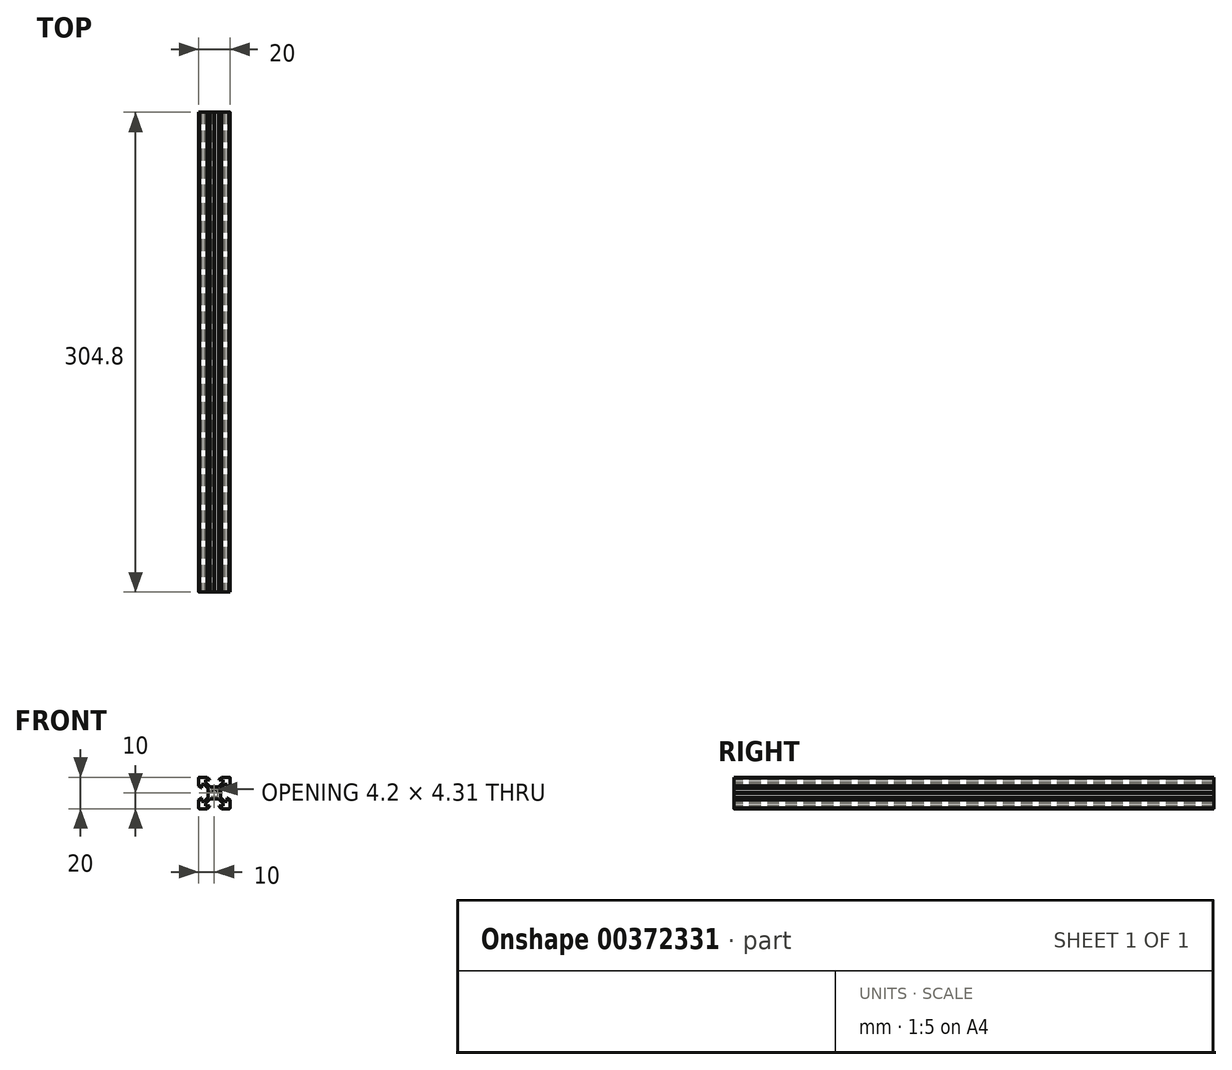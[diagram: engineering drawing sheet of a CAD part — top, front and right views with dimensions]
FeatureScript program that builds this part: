
annotation { "Feature Type Name" : "Feature", "Feature Type Description" : "" }
export const myFeature = defineFeature(function(context is Context, id is Id, definition is map)
    precondition{}
    {
        {
            var Q0;
            Q0=qCreatedBy(makeId("Front.planeOp"),FACE);
            var sketch = newSketch(context, id + "F0", { "sketchPlane" : qUnion([Q0])});
            skFitSpline(sketch, "E0.0", {"points": [v(-8.2, 3.13) * mm, v(-8.2, 3.92) * mm, v(-8.2, 4.7) * mm, v(-8.2, 5.5) * mm]});
            skFitSpline(sketch, "E0.1", {"points": [v(-8.2, 5.5) * mm, v(-7.65, 5.5) * mm, v(-7.1, 5.5) * mm, v(-6.56, 5.5) * mm]});
            skFitSpline(sketch, "E0.2", {"points": [v(-6.56, 5.5) * mm, v(-5.67, 4.61) * mm, v(-4.79, 3.73) * mm, v(-3.9, 2.84) * mm]});
            skFitSpline(sketch, "E0.3", {"points": [v(-2.84, 3.9) * mm, v(-3.73, 4.79) * mm, v(-4.61, 5.67) * mm, v(-5.5, 6.56) * mm]});
            skFitSpline(sketch, "E0.4", {"points": [v(-5.5, 6.56) * mm, v(-5.5, 7.1) * mm, v(-5.5, 7.65) * mm, v(-5.5, 8.2) * mm]});
            skFitSpline(sketch, "E0.5", {"points": [v(-5.5, 8.2) * mm, v(-4.7, 8.2) * mm, v(-3.92, 8.2) * mm, v(-3.12, 8.2) * mm]});
            skFitSpline(sketch, "E0.6", {"points": [v(-3.12, 8.2) * mm, v(-3.12, 8.32) * mm, v(-3.12, 8.43) * mm, v(-3.12, 8.55) * mm]});
            skFitSpline(sketch, "E0.7", {"points": [v(-10, 4.58) * mm, v(-9.51, 4.1) * mm, v(-9.03, 3.61) * mm, v(-8.54, 3.13) * mm]});
            skFitSpline(sketch, "E0.8", {"points": [v(-8.54, 3.13) * mm, v(-8.43, 3.13) * mm, v(-8.31, 3.13) * mm, v(-8.2, 3.13) * mm]});
            skFitSpline(sketch, "E0.9", {"points": [v(-10, 9.5) * mm, v(-10, 7.86) * mm, v(-10, 6.22) * mm, v(-10, 4.58) * mm]});
            skFitSpline(sketch, "E0.10", {"points": [v(-9.5, 10) * mm, v(-9.57, 10) * mm, v(-9.63, 9.99) * mm, v(-9.7, 9.96) * mm, v(-9.75, 9.94) * mm, v(-9.8, 9.9) * mm, v(-9.85, 9.85) * mm, v(-9.9, 9.8) * mm, v(-9.94, 9.75) * mm, v(-9.96, 9.7) * mm, v(-9.99, 9.63) * mm, v(-10, 9.57) * mm, v(-10, 9.5) * mm]});
            skFitSpline(sketch, "E0.11", {"points": [v(-4.58, 10) * mm, v(-6.22, 10) * mm, v(-7.86, 10) * mm, v(-9.5, 10) * mm]});
            skFitSpline(sketch, "E0.12", {"points": [v(-3.9, 2.84) * mm, v(-3.9, 1.96) * mm, v(-3.9, 1.09) * mm, v(-3.9, 0.21) * mm]});
            skFitSpline(sketch, "E0.13", {"points": [v(-3.9, 0.21) * mm, v(-3.83, 0.14) * mm, v(-3.76, 0.07) * mm, v(-3.69, 0) * mm]});
            skFitSpline(sketch, "E0.14", {"points": [v(-0.2, 3.9) * mm, v(-1.09, 3.9) * mm, v(-1.96, 3.9) * mm, v(-2.84, 3.9) * mm]});
            skFitSpline(sketch, "E0.15", {"points": [v(0, 3.7) * mm, v(-0.07, 3.76) * mm, v(-0.14, 3.83) * mm, v(-0.2, 3.9) * mm]});
            skFitSpline(sketch, "E0.16", {"points": [v(2.1, 0) * mm, v(2.1, 0.27) * mm, v(2, 0.82) * mm, v(1.52, 1.52) * mm, v(0.82, 2) * mm, v(0, 2.15) * mm, v(-0.82, 2) * mm, v(-1.52, 1.52) * mm, v(-2, 0.82) * mm, v(-2.1, 0.27) * mm, v(-2.1, 0) * mm]});
            skFitSpline(sketch, "E1.0", {"points": [v(-8.2, 3.13) * mm, v(-8.2, 3.92) * mm, v(-8.2, 4.7) * mm, v(-8.2, 5.5) * mm]});
            skFitSpline(sketch, "E1.1", {"points": [v(-8.2, 5.5) * mm, v(-7.65, 5.5) * mm, v(-7.1, 5.5) * mm, v(-6.56, 5.5) * mm]});
            skFitSpline(sketch, "E1.2", {"points": [v(-6.56, 5.5) * mm, v(-5.67, 4.61) * mm, v(-4.79, 3.73) * mm, v(-3.9, 2.84) * mm]});
            skFitSpline(sketch, "E1.3", {"points": [v(-2.84, 3.9) * mm, v(-3.73, 4.79) * mm, v(-4.61, 5.67) * mm, v(-5.5, 6.56) * mm]});
            skFitSpline(sketch, "E1.4", {"points": [v(-5.5, 6.56) * mm, v(-5.5, 7.1) * mm, v(-5.5, 7.65) * mm, v(-5.5, 8.2) * mm]});
            skFitSpline(sketch, "E1.5", {"points": [v(-5.5, 8.2) * mm, v(-4.7, 8.2) * mm, v(-3.92, 8.2) * mm, v(-3.12, 8.2) * mm]});
            skFitSpline(sketch, "E1.6", {"points": [v(-3.12, 8.2) * mm, v(-3.12, 8.32) * mm, v(-3.12, 8.43) * mm, v(-3.12, 8.55) * mm]});
            skFitSpline(sketch, "E1.7", {"points": [v(-10, 4.58) * mm, v(-9.51, 4.1) * mm, v(-9.03, 3.61) * mm, v(-8.54, 3.13) * mm]});
            skFitSpline(sketch, "E1.8", {"points": [v(-8.54, 3.13) * mm, v(-8.43, 3.13) * mm, v(-8.31, 3.13) * mm, v(-8.2, 3.13) * mm]});
            skFitSpline(sketch, "E1.9", {"points": [v(-10, 9.5) * mm, v(-10, 7.86) * mm, v(-10, 6.22) * mm, v(-10, 4.58) * mm]});
            skFitSpline(sketch, "E1.10", {"points": [v(-9.5, 10) * mm, v(-9.57, 10) * mm, v(-9.63, 9.99) * mm, v(-9.7, 9.96) * mm, v(-9.75, 9.94) * mm, v(-9.8, 9.9) * mm, v(-9.85, 9.85) * mm, v(-9.9, 9.8) * mm, v(-9.94, 9.75) * mm, v(-9.96, 9.7) * mm, v(-9.99, 9.63) * mm, v(-10, 9.57) * mm, v(-10, 9.5) * mm]});
            skFitSpline(sketch, "E1.11", {"points": [v(-4.58, 10) * mm, v(-6.22, 10) * mm, v(-7.86, 10) * mm, v(-9.5, 10) * mm]});
            skFitSpline(sketch, "E1.12", {"points": [v(-3.9, 2.84) * mm, v(-3.9, 1.96) * mm, v(-3.9, 1.09) * mm, v(-3.9, 0.21) * mm]});
            skFitSpline(sketch, "E1.13", {"points": [v(-3.9, 0.21) * mm, v(-3.83, 0.14) * mm, v(-3.76, 0.07) * mm, v(-3.69, 0) * mm]});
            skFitSpline(sketch, "E1.14", {"points": [v(-0.2, 3.9) * mm, v(-1.09, 3.9) * mm, v(-1.96, 3.9) * mm, v(-2.84, 3.9) * mm]});
            skFitSpline(sketch, "E1.15", {"points": [v(0, 3.7) * mm, v(-0.07, 3.76) * mm, v(-0.14, 3.83) * mm, v(-0.2, 3.9) * mm]});
            skFitSpline(sketch, "E1.16", {"points": [v(2.1, 0) * mm, v(2.1, 0.27) * mm, v(2, 0.82) * mm, v(1.52, 1.52) * mm, v(0.82, 2) * mm, v(0, 2.15) * mm, v(-0.82, 2) * mm, v(-1.52, 1.52) * mm, v(-2, 0.82) * mm, v(-2.1, 0.27) * mm, v(-2.1, 0) * mm]});
            skFitSpline(sketch, "E2.0", {"points": [v(2.84, 3.9) * mm, v(1.96, 3.9) * mm, v(1.09, 3.9) * mm, v(0.21, 3.9) * mm]});
            skFitSpline(sketch, "E2.1", {"points": [v(0.21, 3.9) * mm, v(0.14, 3.83) * mm, v(0.07, 3.76) * mm, v(0, 3.7) * mm]});
            skFitSpline(sketch, "E2.2", {"points": [v(3.9, 0.2) * mm, v(3.9, 1.09) * mm, v(3.9, 1.96) * mm, v(3.9, 2.84) * mm]});
            skFitSpline(sketch, "E2.3", {"points": [v(3.69, 0) * mm, v(3.76, 0.07) * mm, v(3.83, 0.14) * mm, v(3.9, 0.2) * mm]});
            skFitSpline(sketch, "E2.4", {"points": [v(3.9, 2.84) * mm, v(4.79, 3.73) * mm, v(5.67, 4.61) * mm, v(6.56, 5.5) * mm]});
            skFitSpline(sketch, "E2.5", {"points": [v(5.5, 6.56) * mm, v(4.61, 5.67) * mm, v(3.73, 4.79) * mm, v(2.84, 3.9) * mm]});
            skFitSpline(sketch, "E2.6", {"points": [v(6.56, 5.5) * mm, v(7.1, 5.5) * mm, v(7.65, 5.5) * mm, v(8.2, 5.5) * mm]});
            skFitSpline(sketch, "E2.7", {"points": [v(8.2, 5.5) * mm, v(8.2, 4.7) * mm, v(8.2, 3.92) * mm, v(8.2, 3.13) * mm]});
            skFitSpline(sketch, "E2.8", {"points": [v(8.2, 3.13) * mm, v(8.31, 3.13) * mm, v(8.43, 3.13) * mm, v(8.54, 3.13) * mm]});
            skFitSpline(sketch, "E2.9", {"points": [v(8.54, 3.13) * mm, v(9.03, 3.61) * mm, v(9.51, 4.1) * mm, v(10, 4.58) * mm]});
            skFitSpline(sketch, "E2.10", {"points": [v(10, 4.58) * mm, v(10, 6.22) * mm, v(10, 7.86) * mm, v(10, 9.5) * mm]});
            skFitSpline(sketch, "E2.11", {"points": [v(5.5, 8.2) * mm, v(5.5, 7.65) * mm, v(5.5, 7.1) * mm, v(5.5, 6.56) * mm]});
            skFitSpline(sketch, "E2.12", {"points": [v(3.13, 8.2) * mm, v(3.92, 8.2) * mm, v(4.7, 8.2) * mm, v(5.5, 8.2) * mm]});
            skFitSpline(sketch, "E2.13", {"points": [v(3.13, 8.55) * mm, v(3.13, 8.43) * mm, v(3.13, 8.32) * mm, v(3.13, 8.2) * mm]});
            skFitSpline(sketch, "E2.14", {"points": [v(9.5, 10) * mm, v(7.86, 10) * mm, v(6.22, 10) * mm, v(4.58, 10) * mm]});
            skFitSpline(sketch, "E2.15", {"points": [v(10, 9.5) * mm, v(10, 9.57) * mm, v(9.99, 9.63) * mm, v(9.96, 9.7) * mm, v(9.94, 9.75) * mm, v(9.9, 9.8) * mm, v(9.85, 9.85) * mm, v(9.8, 9.9) * mm, v(9.75, 9.94) * mm, v(9.7, 9.96) * mm, v(9.63, 9.99) * mm, v(9.57, 10) * mm, v(9.5, 10) * mm]});
            skFitSpline(sketch, "E2.16", {"points": [v(4.58, 10) * mm, v(4.1, 9.52) * mm, v(3.61, 9.03) * mm, v(3.13, 8.55) * mm]});
            skLineSegment(sketch, "E3", {"start": v(-4.58, 10) * mm, "end": v(-3.12, 8.55) * mm});
            skFitSpline(sketch, "E4.MirrorCS", {"points": [v(-3.9, -0.2) * mm, v(-3.83, -0.14) * mm, v(-3.76, -0.07) * mm, v(-3.69, 0) * mm]});
            skFitSpline(sketch, "E5.MirrorCS", {"points": [v(0, -3.7) * mm, v(-0.07, -3.76) * mm, v(-0.14, -3.83) * mm, v(-0.21, -3.9) * mm]});
            skFitSpline(sketch, "E6.MirrorCS", {"points": [v(-8.55, -3.12) * mm, v(-8.43, -3.12) * mm, v(-8.32, -3.12) * mm, v(-8.2, -3.12) * mm]});
            skFitSpline(sketch, "E7.MirrorCS", {"points": [v(0.2, -3.9) * mm, v(0.14, -3.83) * mm, v(0.07, -3.76) * mm, v(0, -3.7) * mm]});
            skFitSpline(sketch, "E8.MirrorCS", {"points": [v(-3.13, -8.2) * mm, v(-3.13, -8.31) * mm, v(-3.13, -8.43) * mm, v(-3.13, -8.54) * mm]});
            skFitSpline(sketch, "E9.MirrorCS", {"points": [v(-3.9, -0.2) * mm, v(-3.83, -0.14) * mm, v(-3.76, -0.07) * mm, v(-3.69, 0) * mm]});
            skFitSpline(sketch, "E10.MirrorCS", {"points": [v(-8.55, -3.12) * mm, v(-8.43, -3.12) * mm, v(-8.32, -3.12) * mm, v(-8.2, -3.12) * mm]});
            skFitSpline(sketch, "E11.MirrorCS", {"points": [v(0, -3.7) * mm, v(-0.07, -3.76) * mm, v(-0.14, -3.83) * mm, v(-0.21, -3.9) * mm]});
            skFitSpline(sketch, "E12.MirrorCS", {"points": [v(-3.13, -8.2) * mm, v(-3.13, -8.31) * mm, v(-3.13, -8.43) * mm, v(-3.13, -8.54) * mm]});
            skFitSpline(sketch, "E13.MirrorCS", {"points": [v(3.12, -8.55) * mm, v(3.12, -8.43) * mm, v(3.12, -8.32) * mm, v(3.12, -8.2) * mm]});
            skFitSpline(sketch, "E14.MirrorCS", {"points": [v(3.69, 0) * mm, v(3.76, -0.07) * mm, v(3.83, -0.14) * mm, v(3.9, -0.21) * mm]});
            skFitSpline(sketch, "E15.MirrorCS", {"points": [v(8.2, -3.13) * mm, v(8.31, -3.13) * mm, v(8.43, -3.13) * mm, v(8.54, -3.13) * mm]});
            skFitSpline(sketch, "E16.MirrorCS", {"points": [v(-8.2, -5.5) * mm, v(-7.65, -5.5) * mm, v(-7.1, -5.5) * mm, v(-6.56, -5.5) * mm]});
            skFitSpline(sketch, "E17.MirrorCS", {"points": [v(-2.84, -3.9) * mm, v(-3.73, -4.79) * mm, v(-4.61, -5.67) * mm, v(-5.5, -6.56) * mm]});
            skFitSpline(sketch, "E18.MirrorCS", {"points": [v(-5.5, -8.2) * mm, v(-4.7, -8.2) * mm, v(-3.92, -8.2) * mm, v(-3.13, -8.2) * mm]});
            skFitSpline(sketch, "E19.MirrorCS", {"points": [v(-5.5, -6.56) * mm, v(-5.5, -7.1) * mm, v(-5.5, -7.65) * mm, v(-5.5, -8.2) * mm]});
            skFitSpline(sketch, "E20.MirrorCS", {"points": [v(-0.21, -3.9) * mm, v(-1.09, -3.9) * mm, v(-1.96, -3.9) * mm, v(-2.84, -3.9) * mm]});
            skFitSpline(sketch, "E21.MirrorCS", {"points": [v(-8.2, -3.12) * mm, v(-8.2, -3.92) * mm, v(-8.2, -4.7) * mm, v(-8.2, -5.5) * mm]});
            skFitSpline(sketch, "E22.MirrorCS", {"points": [v(-10, -4.58) * mm, v(-9.52, -4.1) * mm, v(-9.03, -3.6) * mm, v(-8.55, -3.12) * mm]});
            skFitSpline(sketch, "E23.MirrorCS", {"points": [v(-10, -9.5) * mm, v(-10, -7.86) * mm, v(-10, -6.22) * mm, v(-10, -4.58) * mm]});
            skFitSpline(sketch, "E24.MirrorCS", {"points": [v(-9.5, -10) * mm, v(-9.57, -10) * mm, v(-9.63, -9.99) * mm, v(-9.7, -9.96) * mm, v(-9.75, -9.94) * mm, v(-9.8, -9.9) * mm, v(-9.85, -9.85) * mm, v(-9.9, -9.8) * mm, v(-9.94, -9.75) * mm, v(-9.96, -9.7) * mm, v(-9.99, -9.63) * mm, v(-10, -9.57) * mm, v(-10, -9.5) * mm]});
            skFitSpline(sketch, "E25.MirrorCS", {"points": [v(-4.58, -10) * mm, v(-6.22, -10) * mm, v(-7.86, -10) * mm, v(-9.5, -10) * mm]});
            skFitSpline(sketch, "E26.MirrorCS", {"points": [v(-3.9, -2.84) * mm, v(-3.9, -1.96) * mm, v(-3.9, -1.09) * mm, v(-3.9, -0.21) * mm]});
            skFitSpline(sketch, "E27.MirrorCS", {"points": [v(-6.56, -5.5) * mm, v(-5.67, -4.61) * mm, v(-4.79, -3.73) * mm, v(-3.9, -2.84) * mm]});
            skFitSpline(sketch, "E28.MirrorCS", {"points": [v(2.1, 0) * mm, v(2.1, -0.27) * mm, v(2, -0.82) * mm, v(1.52, -1.52) * mm, v(0.82, -2) * mm, v(0, -2.15) * mm, v(-0.82, -2) * mm, v(-1.52, -1.52) * mm, v(-2, -0.82) * mm, v(-2.1, -0.27) * mm, v(-2.1, 0) * mm]});
            skFitSpline(sketch, "E29.MirrorCS", {"points": [v(4.58, -10) * mm, v(4.1, -9.52) * mm, v(3.6, -9.03) * mm, v(3.12, -8.55) * mm]});
            skFitSpline(sketch, "E30.MirrorCS", {"points": [v(-6.56, -5.5) * mm, v(-5.67, -4.61) * mm, v(-4.79, -3.73) * mm, v(-3.9, -2.84) * mm]});
            skFitSpline(sketch, "E31.MirrorCS", {"points": [v(10, -4.58) * mm, v(10, -6.22) * mm, v(10, -7.86) * mm, v(10, -9.5) * mm]});
            skLineSegment(sketch, "E32.MirrorCS", {"start": v(-4.58, -10) * mm, "end": v(-3.13, -8.54) * mm});
            skFitSpline(sketch, "E33.MirrorCS", {"points": [v(-4.58, -10) * mm, v(-6.22, -10) * mm, v(-7.86, -10) * mm, v(-9.5, -10) * mm]});
            skFitSpline(sketch, "E34.MirrorCS", {"points": [v(6.56, -5.5) * mm, v(7.1, -5.5) * mm, v(7.65, -5.5) * mm, v(8.2, -5.5) * mm]});
            skFitSpline(sketch, "E35.MirrorCS", {"points": [v(-10, -4.58) * mm, v(-9.52, -4.1) * mm, v(-9.03, -3.6) * mm, v(-8.55, -3.12) * mm]});
            skFitSpline(sketch, "E36.MirrorCS", {"points": [v(-5.5, -6.56) * mm, v(-5.5, -7.1) * mm, v(-5.5, -7.65) * mm, v(-5.5, -8.2) * mm]});
            skFitSpline(sketch, "E37.MirrorCS", {"points": [v(3.12, -8.2) * mm, v(3.92, -8.2) * mm, v(4.7, -8.2) * mm, v(5.5, -8.2) * mm]});
            skFitSpline(sketch, "E38.MirrorCS", {"points": [v(-8.2, -5.5) * mm, v(-7.65, -5.5) * mm, v(-7.1, -5.5) * mm, v(-6.56, -5.5) * mm]});
            skFitSpline(sketch, "E39.MirrorCS", {"points": [v(-8.2, -3.12) * mm, v(-8.2, -3.92) * mm, v(-8.2, -4.7) * mm, v(-8.2, -5.5) * mm]});
            skFitSpline(sketch, "E40.MirrorCS", {"points": [v(10, -9.5) * mm, v(10, -9.57) * mm, v(9.99, -9.63) * mm, v(9.96, -9.7) * mm, v(9.94, -9.75) * mm, v(9.9, -9.8) * mm, v(9.85, -9.85) * mm, v(9.8, -9.9) * mm, v(9.75, -9.94) * mm, v(9.7, -9.96) * mm, v(9.63, -9.99) * mm, v(9.57, -10) * mm, v(9.5, -10) * mm]});
            skFitSpline(sketch, "E41.MirrorCS", {"points": [v(2.1, 0) * mm, v(2.1, -0.27) * mm, v(2, -0.82) * mm, v(1.52, -1.52) * mm, v(0.82, -2) * mm, v(0, -2.15) * mm, v(-0.82, -2) * mm, v(-1.52, -1.52) * mm, v(-2, -0.82) * mm, v(-2.1, -0.27) * mm, v(-2.1, 0) * mm]});
            skFitSpline(sketch, "E42.MirrorCS", {"points": [v(2.84, -3.9) * mm, v(1.96, -3.9) * mm, v(1.09, -3.9) * mm, v(0.2, -3.9) * mm]});
            skFitSpline(sketch, "E43.MirrorCS", {"points": [v(-10, -9.5) * mm, v(-10, -7.86) * mm, v(-10, -6.22) * mm, v(-10, -4.58) * mm]});
            skFitSpline(sketch, "E44.MirrorCS", {"points": [v(8.2, -5.5) * mm, v(8.2, -4.7) * mm, v(8.2, -3.92) * mm, v(8.2, -3.13) * mm]});
            skFitSpline(sketch, "E45.MirrorCS", {"points": [v(8.54, -3.13) * mm, v(9.03, -3.61) * mm, v(9.51, -4.1) * mm, v(10, -4.58) * mm]});
            skFitSpline(sketch, "E46.MirrorCS", {"points": [v(3.9, -2.84) * mm, v(4.79, -3.73) * mm, v(5.67, -4.61) * mm, v(6.56, -5.5) * mm]});
            skFitSpline(sketch, "E47.MirrorCS", {"points": [v(-9.5, -10) * mm, v(-9.57, -10) * mm, v(-9.63, -9.99) * mm, v(-9.7, -9.96) * mm, v(-9.75, -9.94) * mm, v(-9.8, -9.9) * mm, v(-9.85, -9.85) * mm, v(-9.9, -9.8) * mm, v(-9.94, -9.75) * mm, v(-9.96, -9.7) * mm, v(-9.99, -9.63) * mm, v(-10, -9.57) * mm, v(-10, -9.5) * mm]});
            skFitSpline(sketch, "E48.MirrorCS", {"points": [v(-0.21, -3.9) * mm, v(-1.09, -3.9) * mm, v(-1.96, -3.9) * mm, v(-2.84, -3.9) * mm]});
            skFitSpline(sketch, "E49.MirrorCS", {"points": [v(5.5, -6.56) * mm, v(4.61, -5.67) * mm, v(3.73, -4.79) * mm, v(2.84, -3.9) * mm]});
            skFitSpline(sketch, "E50.MirrorCS", {"points": [v(-2.84, -3.9) * mm, v(-3.73, -4.79) * mm, v(-4.61, -5.67) * mm, v(-5.5, -6.56) * mm]});
            skFitSpline(sketch, "E51.MirrorCS", {"points": [v(-5.5, -8.2) * mm, v(-4.7, -8.2) * mm, v(-3.92, -8.2) * mm, v(-3.13, -8.2) * mm]});
            skFitSpline(sketch, "E52.MirrorCS", {"points": [v(5.5, -8.2) * mm, v(5.5, -7.65) * mm, v(5.5, -7.1) * mm, v(5.5, -6.56) * mm]});
            skFitSpline(sketch, "E53.MirrorCS", {"points": [v(3.9, -0.21) * mm, v(3.9, -1.09) * mm, v(3.9, -1.96) * mm, v(3.9, -2.84) * mm]});
            skFitSpline(sketch, "E54.MirrorCS", {"points": [v(-3.9, -2.84) * mm, v(-3.9, -1.96) * mm, v(-3.9, -1.09) * mm, v(-3.9, -0.21) * mm]});
            skFitSpline(sketch, "E55.MirrorCS", {"points": [v(9.5, -10) * mm, v(7.86, -10) * mm, v(6.22, -10) * mm, v(4.58, -10) * mm]});
            skLineSegment(sketch, "E56.MirrorCS", {"start": v(0, 3.7) * mm, "end": v(0, 0) * mm, "construction": true});
            skLineSegment(sketch, "E57.MirrorCS", {"start": v(0, -3.7) * mm, "end": v(0, 0) * mm, "construction": true});
            skSolve(sketch);
        }
        {
            var Q0;
            Q0=qSketchRegion(id+"F0",true);
            extrude(context, id + "F1", {"entities" : qUnion([Q0]), "oppositeDirection" : true, "depth" : 304.8 * mm});
        }
    });
